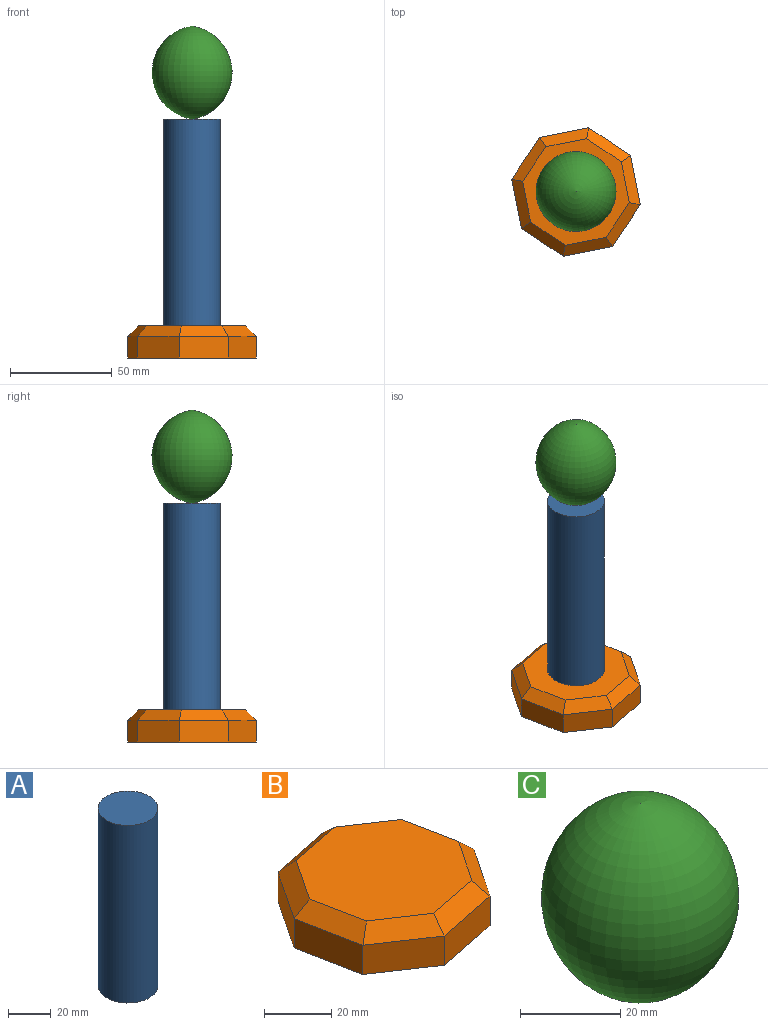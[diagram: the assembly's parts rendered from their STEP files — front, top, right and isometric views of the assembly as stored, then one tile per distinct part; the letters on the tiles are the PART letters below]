
ASSEMBLY  parts=3 mates=2
PART A: 3 faces, bbox 27.9x27.9x101.6 mm
  f0: plane 27.94x27.94mm, normal (0,0,-1), area 613.1mm2, adj f1
  f1: cylinder r=13.97mm len=101.6mm, axis (0,0,-1), area 8918.1mm2, adj f0,f2
  f2: plane 27.94x27.94mm, normal (0,0,1), area 613.1mm2, adj f1
PART B: 18 faces, bbox 63.2x63.2x15.7 mm
  f0: plane 20.5x13.71mm, normal (-0.56,-0.83,0), area 263.1mm2, adj f1,f7,f9,f16
  f1: plane 24.19x10.67mm, normal (0.19,-0.98,0), area 263.1mm2, adj f0,f2,f9,f17
  f2: plane 20.5x13.71mm, normal (0.83,-0.56,0), area 263.1mm2, adj f1,f3,f9,f15
  f3: plane 24.19x10.67mm, normal (0.98,0.19,0), area 263.1mm2, adj f2,f4,f9,f13
  f4: plane 20.5x13.71mm, normal (0.56,0.83,0), area 263.1mm2, adj f3,f5,f9,f11
  f5: plane 24.19x10.67mm, normal (-0.19,0.98,0), area 263.1mm2, adj f4,f6,f9,f10
  f6: plane 20.5x13.71mm, normal (-0.83,0.56,0), area 263.1mm2, adj f5,f7,f9,f12
  f7: plane 24.19x10.67mm, normal (-0.98,-0.19,0), area 263.1mm2, adj f0,f6,f9,f14
  f8: plane 52.43x52.43mm, normal (0,0,1), area 2020.7mm2, adj f10,f11,f12,f13,f14,f15,f16,f17
  f9: plane 63.21x63.21mm, normal (0,0,-1), area 2937.6mm2, adj f0,f1,f2,f3,f4,f5,f6,f7
  f10: plane 24.19x9.38mm, normal (-0.14,0.69,0.71), area 162.1mm2, adj f5,f8,f11,f12
  f11: plane 21.58x16.76mm, normal (0.39,0.59,0.71), area 162.1mm2, adj f4,f8,f10,f13
  f12: plane 21.58x16.76mm, normal (-0.59,0.39,0.71), area 162.1mm2, adj f6,f8,f10,f14
  f13: plane 24.19x9.38mm, normal (0.69,0.14,0.71), area 162.1mm2, adj f3,f8,f11,f15
  f14: plane 24.19x9.38mm, normal (-0.69,-0.14,0.71), area 162.1mm2, adj f7,f8,f12,f16
  f15: plane 21.58x16.76mm, normal (0.59,-0.39,0.71), area 162.1mm2, adj f2,f8,f13,f17
  f16: plane 21.58x16.76mm, normal (-0.39,-0.59,0.71), area 162.1mm2, adj f0,f8,f14,f17
  f17: plane 24.19x9.38mm, normal (0.14,-0.69,0.71), area 162.1mm2, adj f1,f8,f15,f16
PART C: 1 faces, bbox 19.7x0x45.8 mm
  f0: torus R=3.46mm, axis (0,0,-1), area 5240mm2
PLACE A t=(-1.03,-35.88,-36.23)mm
PLACE B t=(-1.03,-33.43,-51.98)mm
PLACE C t=(-1.03,-35.88,69.23)mm
MATE fastened A.f1 <-> B.f8  axis (0,0,-1) through (-1.03,-35.88,-36.23)mm
MATE ball C.f0 <-> A.f1  axis (0,0,-1) through (-1.03,-35.88,65.37)mm
